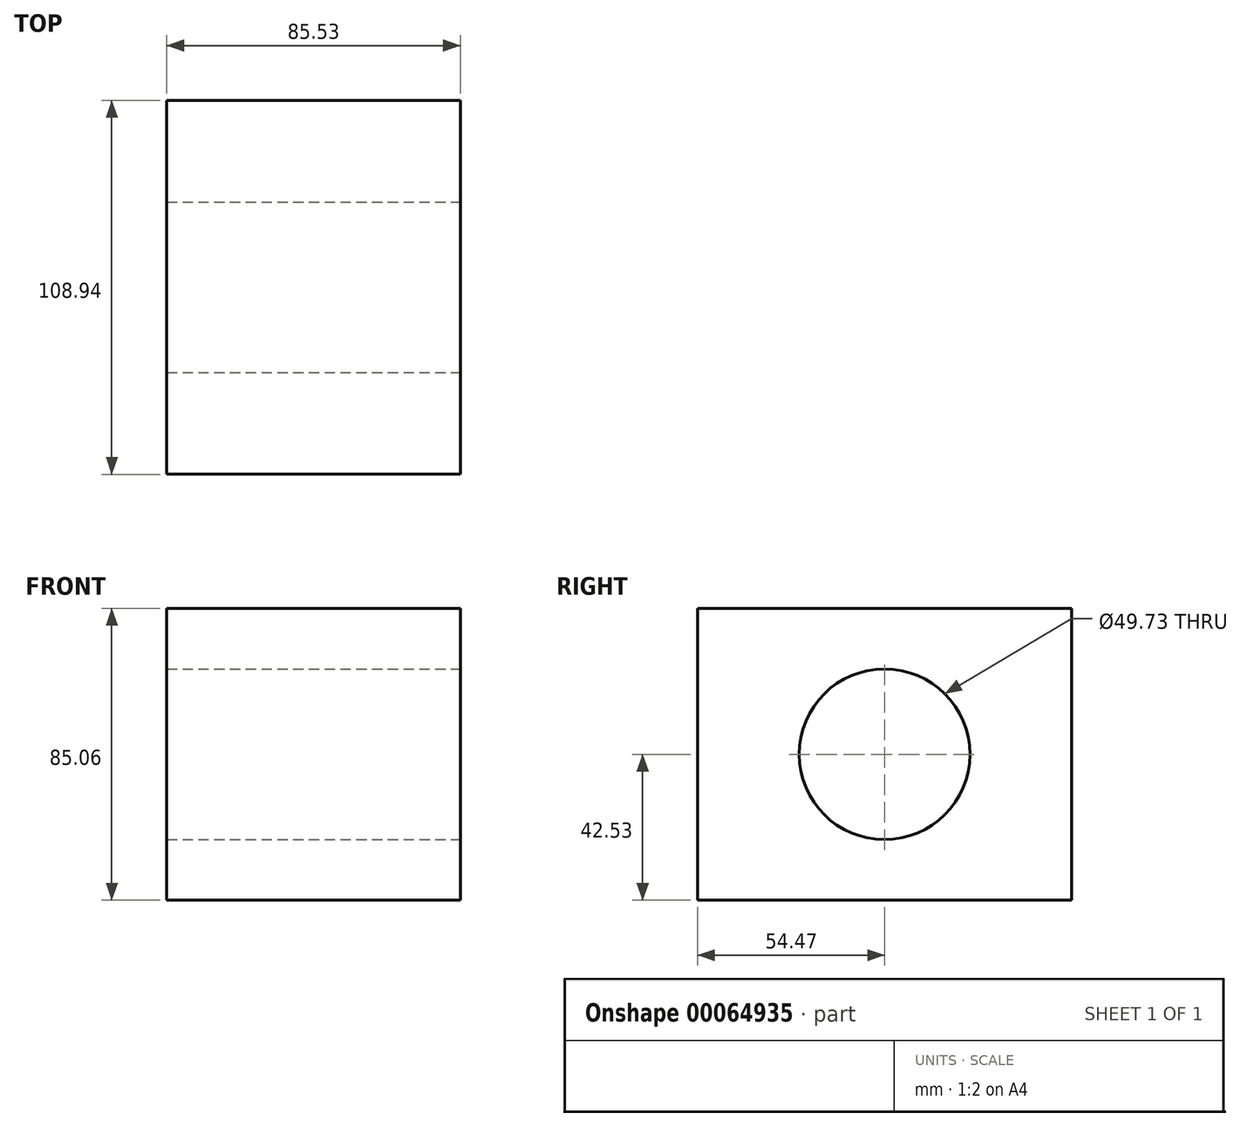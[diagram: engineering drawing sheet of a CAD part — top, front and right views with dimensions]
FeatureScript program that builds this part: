
annotation { "Feature Type Name" : "Feature", "Feature Type Description" : "" }
export const myFeature = defineFeature(function(context is Context, id is Id, definition is map)
    precondition{}
    {
        {
            var Q0;
            Q0=qCreatedBy(makeId("Right.planeOp"),FACE);
            var sketch = newSketch(context, id + "F0", { "sketchPlane" : qUnion([Q0])});
            skLineSegment(sketch, "E0.rect.bottom", {"start": v(-54.47, 42.53) * mm, "end": v(54.47, 42.53) * mm});
            skLineSegment(sketch, "E0.rect.top", {"start": v(-54.47, -42.53) * mm, "end": v(54.47, -42.53) * mm});
            skLineSegment(sketch, "E0.rect.left", {"start": v(-54.47, 42.53) * mm, "end": v(-54.47, -42.53) * mm});
            skLineSegment(sketch, "E0.rect.right", {"start": v(54.47, 42.53) * mm, "end": v(54.47, -42.53) * mm});
            skPoint(sketch, "E0.rect.middle", {"position": v(0, 0) * mm});
            skCircle(sketch, "E1", {"center": v(0, 0) * mm, "radius": 24.86 * mm});
            skSolve(sketch);
        }
        {
            var Q0;
            Q0=makeQuery(id+"F0.imprint","IMPRINT",FACE,{"disambiguationData":[TD([[makeQuery(id+"F0.imprint","IMPRINT",EDGE,{"derivedFrom":sQuery(id+"F0.wireOp",EDGE,"E0.rect.bottom")}),-1.0]])]});
            extrude(context, id + "F1", {"entities" : qUnion([Q0]), "oppositeDirection" : true, "depth" : 85.53 * mm});
        }
    });
